# Revit family: LH-Series Bar Joist
name_source: partatom
category: Structural Framing
revit_build: Autodesk Revit Architecture 2012 (Build: 20110210_1515)
units: mm (PartAtom-declared; Revit-internal decimal feet)

## types (80) — shared parameters
Assembly Code = B1010350
Chord Thickness = 0' - 0 1/2"
Cord Leg = 0' - 2 1/2"
Rendering Material = <By Category>
Seat Depth = 0' - 5"
Seat Length = 0' - 6"
Vertical Member Visibility = Yes
Web Thickness = 0' - 1"

## per-type parameters (varying)
| type | Depth | End Panel | Wt |
| 18LH02 | 1' - 6" | 2' - 3" | 10 |
| 18LH03 | 1' - 6" | 2' - 3" | 11 |
| 18LH04 | 1' - 6" | 2' - 3" | 12 |
| 18LH05 | 1' - 6" | 2' - 3" | 15 |
| 18LH06 | 1' - 6" | 2' - 3" | 15 |
| 18LH07 | 1' - 6" | 2' - 3" | 17 |
| 18LH08 | 1' - 6" | 2' - 3" | 19 |
| 18LH09 | 1' - 6" | 2' - 3" | 21 |
| 20LH02 | 1' - 8" | 2' - 6" | 10 |
| 20LH03 | 1' - 8" | 2' - 6" | 11 |
| 20LH04 | 1' - 8" | 2' - 6" | 12 |
| 20LH05 | 1' - 8" | 2' - 6" | 14 |
| 20LH06 | 1' - 8" | 2' - 6" | 15 |
| 20LH07 | 1' - 8" | 2' - 6" | 17 |
| 20LH08 | 1' - 8" | 2' - 6" | 19 |
| 20LH09 | 1' - 8" | 2' - 6" | 21 |
| 20LH10 | 1' - 8" | 2' - 6" | 23 |
| 24LH03 | 2' - 0" | 3' - 0" | 11 |
| 24LH04 | 2' - 0" | 3' - 0" | 12 |
| 24LH05 | 2' - 0" | 3' - 0" | 13 |
| 24LH06 | 2' - 0" | 3' - 0" | 16 |
| 24LH07 | 2' - 0" | 3' - 0" | 17 |
| 24LH08 | 2' - 0" | 3' - 0" | 18 |
| 24LH09 | 2' - 0" | 3' - 0" | 21 |
| 24LH10 | 2' - 0" | 3' - 0" | 23 |
| 24LH11 | 2' - 0" | 3' - 0" | 25 |
| 28LH05 | 2' - 4" | 3' - 6" | 13 |
| 28LH06 | 2' - 4" | 3' - 6" | 16 |
| 28LH07 | 2' - 4" | 3' - 6" | 17 |
| 28LH08 | 2' - 4" | 3' - 6" | 18 |
| 28LH09 | 2' - 4" | 3' - 6" | 21 |
| 28LH10 | 2' - 4" | 3' - 6" | 23 |
| 28LH11 | 2' - 4" | 3' - 6" | 25 |
| 28LH12 | 2' - 4" | 3' - 6" | 27 |
| 28LH13 | 2' - 4" | 3' - 6" | 30 |
| 32LH06 | 2' - 8" | 4' - 0" | 14 |
| 32LH07 | 2' - 8" | 4' - 0" | 16 |
| 32LH08 | 2' - 8" | 4' - 0" | 17 |
| 32LH09 | 2' - 8" | 4' - 0" | 21 |
| 32LH10 | 2' - 8" | 4' - 0" | 21 |
| 32LH11 | 2' - 8" | 4' - 0" | 24 |
| 32LH12 | 2' - 8" | 4' - 0" | 27 |
| 32LH13 | 2' - 8" | 4' - 0" | 30 |
| 32LH14 | 2' - 8" | 4' - 0" | 33 |
| 32LH15 | 2' - 8" | 4' - 0" | 35 |
| 36LH07 | 3' - 0" | 4' - 6" | 16 |
| 36LH08 | 3' - 0" | 4' - 6" | 18 |
| 36LH09 | 3' - 0" | 4' - 6" | 21 |
| 36LH10 | 3' - 0" | 4' - 6" | 21 |
| 36LH11 | 3' - 0" | 4' - 6" | 23 |
| 36LH12 | 3' - 0" | 4' - 6" | 25 |
| 36LH13 | 3' - 0" | 4' - 6" | 30 |
| 36LH14 | 3' - 0" | 4' - 6" | 36 |
| 36LH15 | 3' - 0" | 4' - 6" | 36 |
| 40LH08 | 3' - 4" | 5' - 0" | 16 |
| 40LH09 | 3' - 4" | 5' - 0" | 21 |
| 40LH10 | 3' - 4" | 5' - 0" | 21 |
| 40LH11 | 3' - 4" | 5' - 0" | 22 |
| 40LH12 | 3' - 4" | 5' - 0" | 25 |
| 40LH13 | 3' - 4" | 5' - 0" | 30 |
| 40LH14 | 3' - 4" | 5' - 0" | 35 |
| 40LH15 | 3' - 4" | 5' - 0" | 36 |
| 40LH16 | 3' - 4" | 5' - 0" | 42 |
| 44LH09 | 3' - 8" | 5' - 6" | 19 |
| 44LH10 | 3' - 8" | 5' - 6" | 21 |
| 44LH11 | 3' - 8" | 5' - 6" | 22 |
| 44LH12 | 3' - 8" | 5' - 6" | 25 |
| 44LH13 | 3' - 8" | 5' - 6" | 30 |
| 44LH14 | 3' - 8" | 5' - 6" | 31 |
| 44LH15 | 3' - 8" | 5' - 6" | 36 |
| 44LH16 | 3' - 8" | 5' - 6" | 42 |
| 44LH17 | 3' - 8" | 5' - 6" | 47 |
| 48LH10 | 4' - 0" | 6' - 0" | 21 |
| 48LH11 | 4' - 0" | 6' - 0" | 22 |
| 48LH12 | 4' - 0" | 6' - 0" | 25 |
| 48LH13 | 4' - 0" | 6' - 0" | 29 |
| 48LH14 | 4' - 0" | 6' - 0" | 32 |
| 48LH15 | 4' - 0" | 6' - 0" | 36 |
| 48LH16 | 4' - 0" | 6' - 0" | 42 |
| 48LH17 | 4' - 0" | 6' - 0" | 47 |

## geometry (parser evidence)
native form markers: Sweep x6
no freeform markers — native parametric forms only
